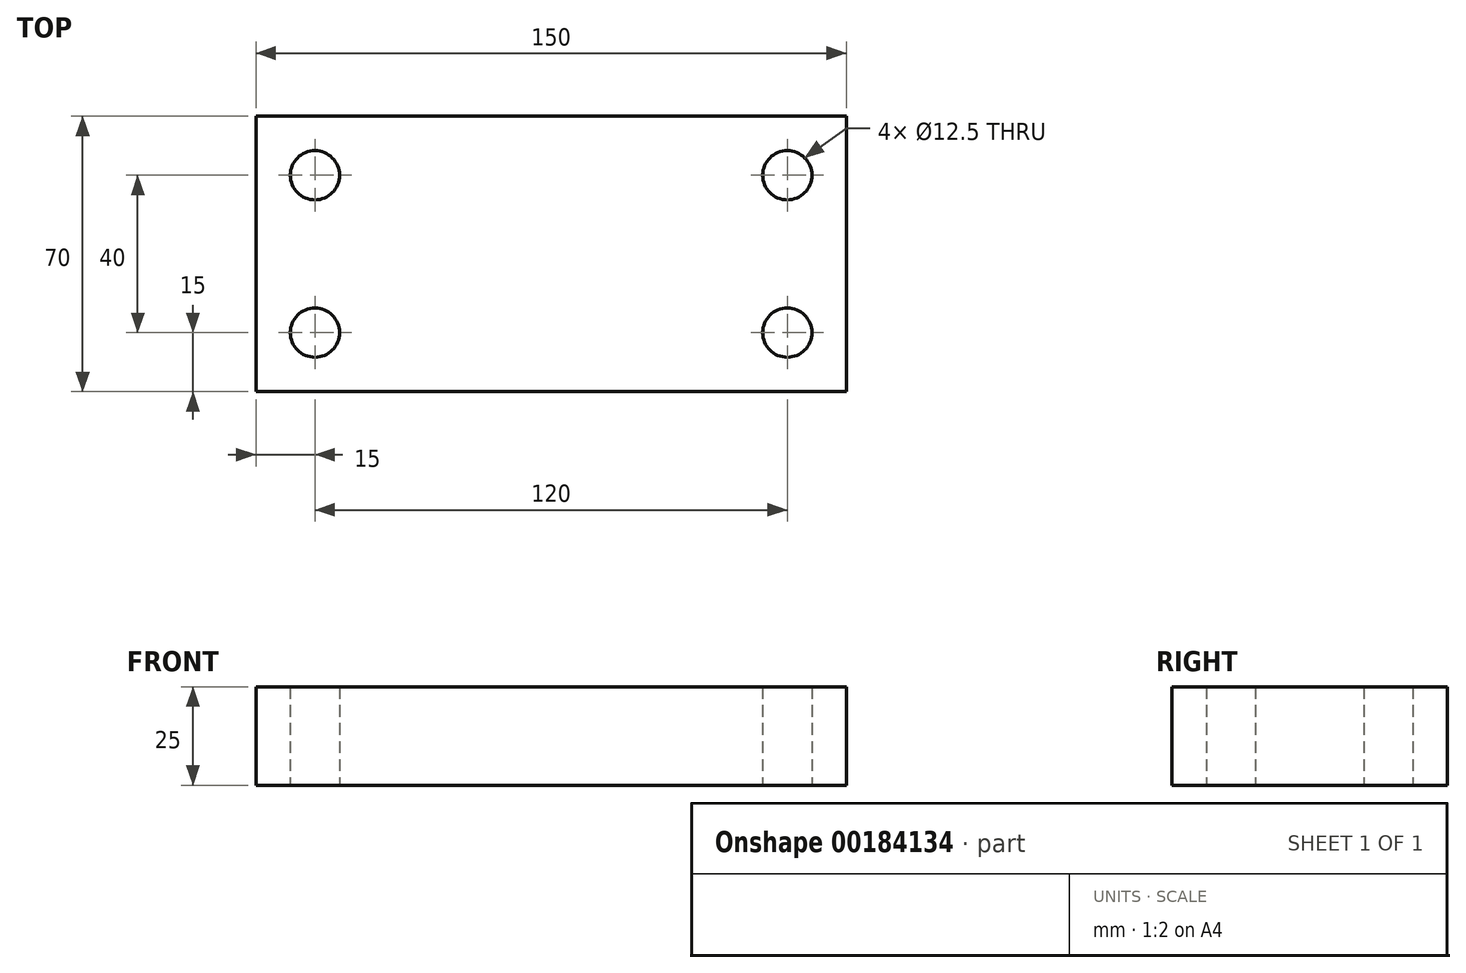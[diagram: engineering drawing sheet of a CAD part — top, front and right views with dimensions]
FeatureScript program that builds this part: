
annotation { "Feature Type Name" : "Feature", "Feature Type Description" : "" }
export const myFeature = defineFeature(function(context is Context, id is Id, definition is map)
    precondition{}
    {
        {
            var Q0;
            Q0=qCreatedBy(makeId("Top.planeOp"),FACE);
            var sketch = newSketch(context, id + "F0", { "sketchPlane" : qUnion([Q0])});
            skLineSegment(sketch, "E0.bottom", {"start": v(-75, 35) * mm, "end": v(75, 35) * mm});
            skLineSegment(sketch, "E0.top", {"start": v(-75, -35) * mm, "end": v(75, -35) * mm});
            skLineSegment(sketch, "E0.left", {"start": v(-75, 35) * mm, "end": v(-75, -35) * mm});
            skLineSegment(sketch, "E0.right", {"start": v(75, 35) * mm, "end": v(75, -35) * mm});
            skPoint(sketch, "E0.middle", {"position": v(0, 0) * mm});
            skLineSegment(sketch, "E1", {"start": v(0, 35) * mm, "end": v(0, -35) * mm, "construction": true});
            skLineSegment(sketch, "E2", {"start": v(-75, 0) * mm, "end": v(75, 0) * mm, "construction": true});
            skLineSegment(sketch, "E3.0", {"start": v(-60, 35) * mm, "end": v(-60, -35) * mm, "construction": true});
            skLineSegment(sketch, "E4.0", {"start": v(-75, 20) * mm, "end": v(75, 20) * mm, "construction": true});
            skCircle(sketch, "E5", {"center": v(-60, 20) * mm, "radius": 6.25 * mm});
            skCircle(sketch, "E6.MirrorC", {"center": v(60, 20) * mm, "radius": 6.25 * mm});
            skCircle(sketch, "E7.MirrorC", {"center": v(-60, -20) * mm, "radius": 6.25 * mm});
            skCircle(sketch, "E8.MirrorC", {"center": v(60, -20) * mm, "radius": 6.25 * mm});
            skSolve(sketch);
        }
        {
            var Q0;
            Q0 = qSketchRegion(id + "F0", true);
            extrude(context, id + "F1", {"entities" : qUnion([Q0]), "depth" : 25 * mm});
        }
    });
